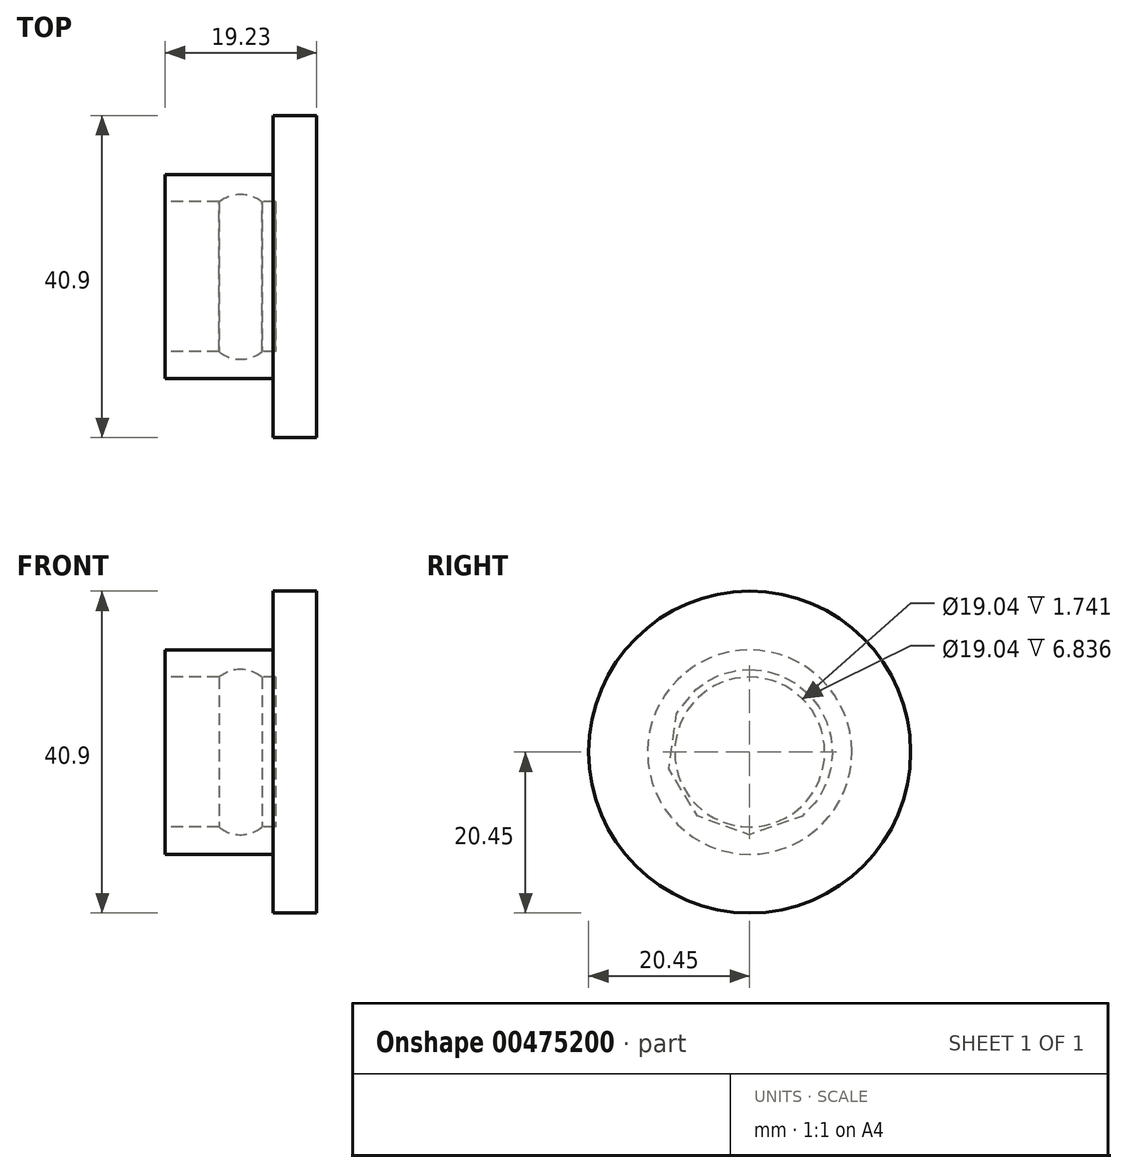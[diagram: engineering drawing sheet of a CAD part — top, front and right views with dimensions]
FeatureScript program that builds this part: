
annotation { "Feature Type Name" : "Feature", "Feature Type Description" : "" }
export const myFeature = defineFeature(function(context is Context, id is Id, definition is map)
    precondition{}
    {
        {
            var Q0;
            Q0=qCreatedBy(makeId("Front.planeOp"),FACE);
            var sketch = newSketch(context, id + "F0", { "sketchPlane" : qUnion([Q0])});
            skPoint(sketch, "E0.start.orphan", {"position": v(-258.76, 0) * mm});
            skPoint(sketch, "E1.start.orphan", {"position": v(-309.56, 0) * mm});
            skPoint(sketch, "E2.start.orphan", {"position": v(0, 25.4) * mm});
            skLineSegment(sketch, "E3", {"start": v(-44.63, 9.52) * mm, "end": v(-44.63, 12.97) * mm});
            skLineSegment(sketch, "E4", {"start": v(-44.63, 12.97) * mm, "end": v(-5.5, 12.97) * mm});
            skLineSegment(sketch, "E5", {"start": v(-5.5, 12.97) * mm, "end": v(-5.5, 20.45) * mm});
            skLineSegment(sketch, "E6", {"start": v(-5.5, 20.45) * mm, "end": v(0, 20.45) * mm});
            skLineSegment(sketch, "E7", {"start": v(0, 20.45) * mm, "end": v(0, 0) * mm});
            skLineSegment(sketch, "E8", {"start": v(-44.63, 9.52) * mm, "end": v(-12.39, 9.52) * mm});
            skLineSegment(sketch, "E9", {"start": v(-5.22, 9.52) * mm, "end": v(-5.22, 0) * mm});
            skLineSegment(sketch, "E10", {"start": v(-5.22, 0) * mm, "end": v(0, 0) * mm});
            skPoint(sketch, "E11.orphan", {"position": v(-44.63, 0) * mm});
            skArc(sketch, "E12", {"start": v(-6.96, 9.52) * mm, "mid": v(-9.68, 10.5) * mm, "end": v(-12.39, 9.52) * mm});
            skLineSegment(sketch, "E13", {"start": v(-6.96, 9.52) * mm, "end": v(-5.22, 9.52) * mm});
            skSolve(sketch);
        }
        {
            var Q0;
            Q0=makeQuery(id+"F0.imprint","IMPRINT",FACE,{"disambiguationData":[TD([[makeQuery(id+"F0.imprint","IMPRINT",EDGE,{"derivedFrom":sQuery(id+"F0.wireOp",EDGE,"E3")}),-1.0]])]});
            var Q1;
            Q1=sQuery(id+"F0.wireOp",EDGE,"E10");
            revolve(context, id + "F1", {"entities" : qUnion([Q0]), "axis" : qUnion([Q1]), "revolveType" : RevolveType.FULL});
        }
        {
            var Q0;
            Q0=makeQuery(id+"F1.opRevolve","SWEPT_FACE",FACE,{"disambiguationData":[OSD([sQuery(id+"F0.wireOp",EDGE,"E3")])]});
            extrude(context, id + "F2", {"entities" : qUnion([Q0]), "operationType" : NewBodyOperationType.REMOVE, "oppositeDirection" : true, "depth" : 25.4 * mm});
        }
    });
